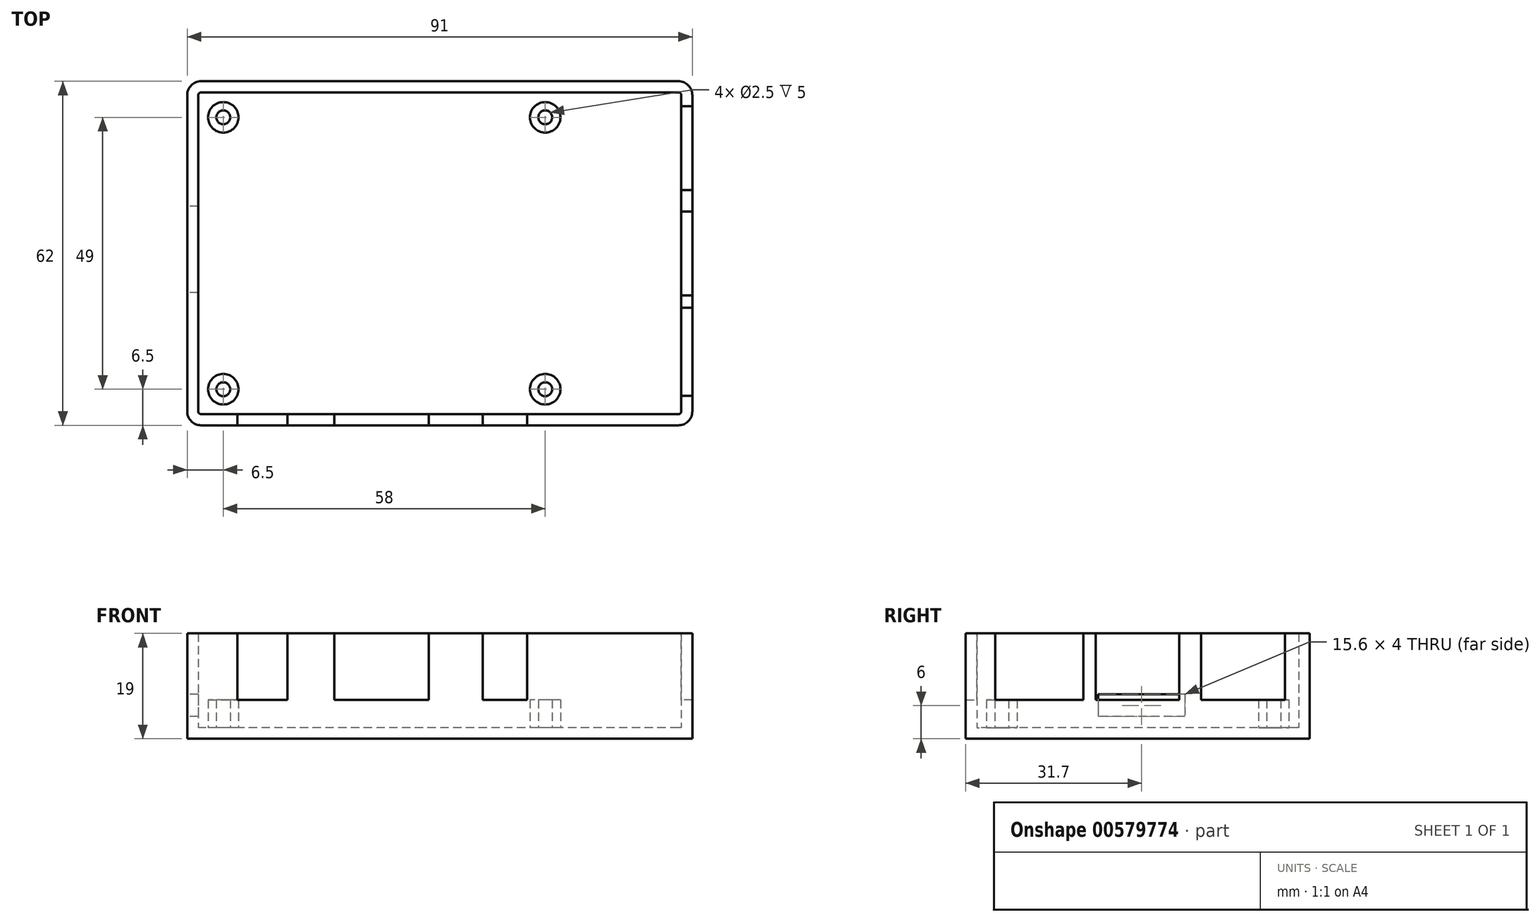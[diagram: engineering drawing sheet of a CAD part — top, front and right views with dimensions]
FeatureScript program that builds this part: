
annotation { "Feature Type Name" : "Feature", "Feature Type Description" : "" }
export const myFeature = defineFeature(function(context is Context, id is Id, definition is map)
    precondition{}
    {
        {
            var Q0;
            Q0=qCreatedBy(makeId("Top.planeOp"),FACE);
            var sketch = newSketch(context, id + "F0", { "sketchPlane" : qUnion([Q0])});
            skLineSegment(sketch, "E0.bottom", {"start": v(2.5, 0) * mm, "end": v(88.5, 0) * mm});
            skLineSegment(sketch, "E0.top", {"start": v(2.5, 62) * mm, "end": v(88.5, 62) * mm});
            skLineSegment(sketch, "E0.left", {"start": v(0, 2.5) * mm, "end": v(0, 59.5) * mm});
            skLineSegment(sketch, "E0.right", {"start": v(91, 2.5) * mm, "end": v(91, 59.5) * mm});
            skPoint(sketch, "E1.visualSharp", {"position": v(0, 62) * mm});
            skArc(sketch, "E1.filletArc", {"start": v(2.5, 62) * mm, "mid": v(0.73, 61.27) * mm, "end": v(0, 59.5) * mm});
            skPoint(sketch, "E2.visualSharp", {"position": v(91, 62) * mm});
            skArc(sketch, "E2.filletArc", {"start": v(91, 59.5) * mm, "mid": v(90.27, 61.27) * mm, "end": v(88.5, 62) * mm});
            skPoint(sketch, "E3.visualSharp", {"position": v(91, 0) * mm});
            skArc(sketch, "E3.filletArc", {"start": v(88.5, 0) * mm, "mid": v(90.27, 0.73) * mm, "end": v(91, 2.5) * mm});
            skPoint(sketch, "E4.visualSharp", {"position": v(0, 0) * mm});
            skArc(sketch, "E4.filletArc", {"start": v(0, 2.5) * mm, "mid": v(0.73, 0.73) * mm, "end": v(2.5, 0) * mm});
            skLineSegment(sketch, "E5.0", {"start": v(2.5, 60) * mm, "end": v(88.5, 60) * mm});
            skArc(sketch, "E5.1", {"start": v(89, 59.5) * mm, "mid": v(88.85, 59.85) * mm, "end": v(88.5, 60) * mm});
            skArc(sketch, "E5.2", {"start": v(2.5, 60) * mm, "mid": v(2.15, 59.85) * mm, "end": v(2, 59.5) * mm});
            skLineSegment(sketch, "E5.3", {"start": v(89, 2.5) * mm, "end": v(89, 59.5) * mm});
            skLineSegment(sketch, "E5.4", {"start": v(2, 2.5) * mm, "end": v(2, 59.5) * mm});
            skArc(sketch, "E5.5", {"start": v(2, 2.5) * mm, "mid": v(2.15, 2.15) * mm, "end": v(2.5, 2) * mm});
            skLineSegment(sketch, "E5.6", {"start": v(2.5, 2) * mm, "end": v(88.5, 2) * mm});
            skArc(sketch, "E5.7", {"start": v(88.5, 2) * mm, "mid": v(88.85, 2.15) * mm, "end": v(89, 2.5) * mm});
            skSolve(sketch);
        }
        {
            var Q0;
            Q0=makeQuery(id+"F0.imprint","IMPRINT",FACE,{"disambiguationData":[TD([[makeQuery(id+"F0.imprint","IMPRINT",EDGE,{"derivedFrom":sQuery(id+"F0.wireOp",EDGE,"E5.0")}),-1.0]])]});
            var Q1;
            Q1=makeQuery(id+"F0.imprint","IMPRINT",FACE,{"disambiguationData":[TD([[makeQuery(id+"F0.imprint","IMPRINT",EDGE,{"derivedFrom":sQuery(id+"F0.wireOp",EDGE,"E0.bottom")}),1.0]])]});
            extrude(context, id + "F1", {"entities" : qUnion([Q0, Q1]), "depth" : 2 * mm, "offsetDistance" : 25 * mm});
        }
        {
            var Q0;
            Q0 = qSketchRegion(id + "F0", true);
            extrude(context, id + "F2", {"entities" : qUnion([Q0]), "operationType" : NewBodyOperationType.ADD, "depth" : 19 * mm, "offsetDistance" : 25 * mm});
        }
        {
            var Q0;
            Q0=makeQuery(id+"F1.opExtrude","CAP_FACE",FACE,{"disambiguationData":[OSD([sQuery(id+"F0.wireOp",EDGE,"E0.bottom"),sQuery(id+"F0.wireOp",EDGE,"E0.top"),sQuery(id+"F0.wireOp",EDGE,"E0.left"),sQuery(id+"F0.wireOp",EDGE,"E0.right"),sQuery(id+"F0.wireOp",EDGE,"E1.filletArc"),sQuery(id+"F0.wireOp",EDGE,"E2.filletArc"),sQuery(id+"F0.wireOp",EDGE,"E3.filletArc"),sQuery(id+"F0.wireOp",EDGE,"E4.filletArc")])],"isStart":false});
            var sketch = newSketch(context, id + "F3", { "sketchPlane" : qUnion([Q0])});
            skCircle(sketch, "E6", {"center": v(6.5, 55.5) * mm, "radius": 2.75 * mm});
            skCircle(sketch, "E7", {"center": v(64.5, 55.5) * mm, "radius": 2.75 * mm});
            skCircle(sketch, "E8", {"center": v(6.5, 6.5) * mm, "radius": 2.75 * mm});
            skCircle(sketch, "E9", {"center": v(64.5, 6.5) * mm, "radius": 2.75 * mm});
            skCircle(sketch, "E10", {"center": v(6.5, 55.5) * mm, "radius": 1.25 * mm});
            skCircle(sketch, "E11", {"center": v(64.5, 55.5) * mm, "radius": 1.25 * mm});
            skCircle(sketch, "E12", {"center": v(64.5, 6.5) * mm, "radius": 1.25 * mm});
            skCircle(sketch, "E13", {"center": v(6.5, 6.5) * mm, "radius": 1.25 * mm});
            skSolve(sketch);
        }
        {
            var Q0;
            Q0 = qSketchRegion(id + "F3", true);
            extrude(context, id + "F4", {"entities" : qUnion([Q0]), "operationType" : NewBodyOperationType.ADD, "depth" : 5 * mm, "offsetDistance" : 25 * mm});
        }
        {
            var Q0;
            Q0=makeQuery(id+"F2.opExtrude","CAP_FACE",FACE,{"disambiguationData":[OSD([sQuery(id+"F0.wireOp",EDGE,"E0.bottom"),sQuery(id+"F0.wireOp",EDGE,"E0.top"),sQuery(id+"F0.wireOp",EDGE,"E0.left"),sQuery(id+"F0.wireOp",EDGE,"E0.right"),sQuery(id+"F0.wireOp",EDGE,"E1.filletArc"),sQuery(id+"F0.wireOp",EDGE,"E2.filletArc"),sQuery(id+"F0.wireOp",EDGE,"E3.filletArc"),sQuery(id+"F0.wireOp",EDGE,"E4.filletArc"),sQuery(id+"F0.wireOp",EDGE,"E5.0"),sQuery(id+"F0.wireOp",EDGE,"E5.1"),sQuery(id+"F0.wireOp",EDGE,"E5.2"),sQuery(id+"F0.wireOp",EDGE,"E5.3"),sQuery(id+"F0.wireOp",EDGE,"E5.4"),sQuery(id+"F0.wireOp",EDGE,"E5.5"),sQuery(id+"F0.wireOp",EDGE,"E5.6"),sQuery(id+"F0.wireOp",EDGE,"E5.7")])],"isStart":false});
            var sketch = newSketch(context, id + "F5", { "sketchPlane" : qUnion([Q0])});
            skLineSegment(sketch, "E14.bottom", {"start": v(9.05, 0) * mm, "end": v(18.05, 0) * mm});
            skLineSegment(sketch, "E14.top", {"start": v(9.05, 2) * mm, "end": v(18.05, 2) * mm});
            skLineSegment(sketch, "E14.left", {"start": v(9.05, 0) * mm, "end": v(9.05, 2) * mm});
            skLineSegment(sketch, "E14.right", {"start": v(18.05, 0) * mm, "end": v(18.05, 2) * mm});
            skLineSegment(sketch, "E15.bottom", {"start": v(26.5, 2) * mm, "end": v(43.5, 2) * mm});
            skLineSegment(sketch, "E15.top", {"start": v(26.5, 0) * mm, "end": v(43.5, 0) * mm});
            skLineSegment(sketch, "E15.left", {"start": v(26.5, 2) * mm, "end": v(26.5, 0) * mm});
            skLineSegment(sketch, "E15.right", {"start": v(43.5, 2) * mm, "end": v(43.5, 0) * mm});
            skLineSegment(sketch, "E16.bottom", {"start": v(53.25, 0) * mm, "end": v(61.25, 0) * mm});
            skLineSegment(sketch, "E16.top", {"start": v(53.25, 2) * mm, "end": v(61.25, 2) * mm});
            skLineSegment(sketch, "E16.left", {"start": v(53.25, 0) * mm, "end": v(53.25, 2) * mm});
            skLineSegment(sketch, "E16.right", {"start": v(61.25, 0) * mm, "end": v(61.25, 2) * mm});
            skLineSegment(sketch, "E17.bottom", {"start": v(91, 5.3) * mm, "end": v(89, 5.3) * mm});
            skLineSegment(sketch, "E17.top", {"start": v(91, 21.2) * mm, "end": v(89, 21.2) * mm});
            skLineSegment(sketch, "E17.left", {"start": v(91, 5.3) * mm, "end": v(91, 21.2) * mm});
            skLineSegment(sketch, "E17.right", {"start": v(89, 5.3) * mm, "end": v(89, 21.2) * mm});
            skLineSegment(sketch, "E18.bottom", {"start": v(89, 23.4) * mm, "end": v(91, 23.4) * mm});
            skLineSegment(sketch, "E18.top", {"start": v(89, 38.5) * mm, "end": v(91, 38.5) * mm});
            skLineSegment(sketch, "E18.left", {"start": v(89, 23.4) * mm, "end": v(89, 38.5) * mm});
            skLineSegment(sketch, "E18.right", {"start": v(91, 23.4) * mm, "end": v(91, 38.5) * mm});
            skLineSegment(sketch, "E19.bottom", {"start": v(91, 42.4) * mm, "end": v(89, 42.4) * mm});
            skLineSegment(sketch, "E19.top", {"start": v(91, 57.5) * mm, "end": v(89, 57.5) * mm});
            skLineSegment(sketch, "E19.left", {"start": v(91, 42.4) * mm, "end": v(91, 57.5) * mm});
            skLineSegment(sketch, "E19.right", {"start": v(89, 42.4) * mm, "end": v(89, 57.5) * mm});
            skSolve(sketch);
        }
        {
            var Q0;
            Q0 = qSketchRegion(id + "F5", true);
            extrude(context, id + "F6", {"entities" : qUnion([Q0]), "operationType" : NewBodyOperationType.REMOVE, "oppositeDirection" : true, "depth" : 12 * mm, "offsetDistance" : 25 * mm});
        }
        {
            var Q0;
            {var subQ0=sQuery(id+"F0.wireOp",EDGE,"E0.left");Q0=makeQuery(id+"F2.boolean.opBoolean","MERGE",FACE,{"derivedFrom":[makeQuery(id+"F1.opExtrude","SWEPT_FACE",FACE,{"disambiguationData":[OSD([subQ0])]}),makeQuery(id+"F2.opExtrude","SWEPT_FACE",FACE,{"disambiguationData":[OSD([subQ0])]})]});}
            var sketch = newSketch(context, id + "F7", { "sketchPlane" : qUnion([Q0])});
            skLineSegment(sketch, "E20.bottom", {"start": v(-39.5, 8) * mm, "end": v(-23.9, 8) * mm});
            skLineSegment(sketch, "E20.top", {"start": v(-39.5, 4) * mm, "end": v(-23.9, 4) * mm});
            skLineSegment(sketch, "E20.left", {"start": v(-39.5, 8) * mm, "end": v(-39.5, 4) * mm});
            skLineSegment(sketch, "E20.right", {"start": v(-23.9, 8) * mm, "end": v(-23.9, 4) * mm});
            skSolve(sketch);
        }
        {
            var Q0;
            Q0 = qSketchRegion(id + "F7", true);
            extrude(context, id + "F8", {"entities" : qUnion([Q0]), "operationType" : NewBodyOperationType.REMOVE, "oppositeDirection" : true, "depth" : 2 * mm, "offsetDistance" : 25 * mm});
        }
    });
